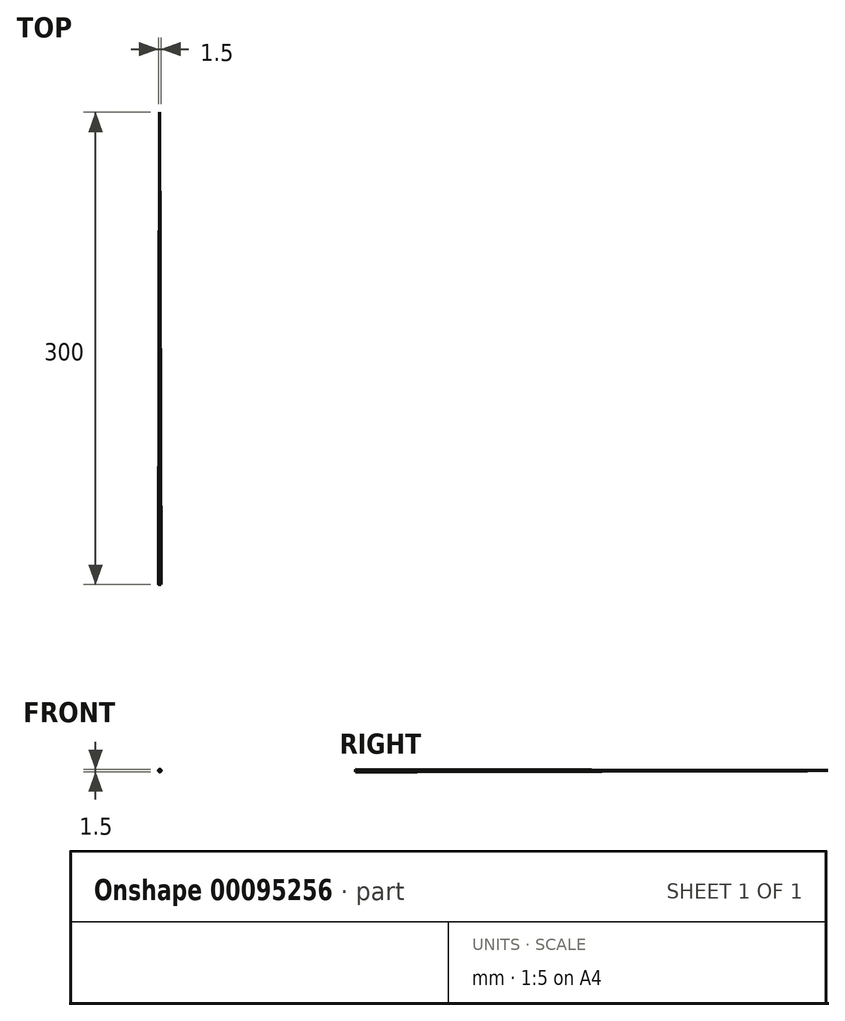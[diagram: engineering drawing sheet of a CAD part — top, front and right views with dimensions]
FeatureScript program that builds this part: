
annotation { "Feature Type Name" : "Feature", "Feature Type Description" : "" }
export const myFeature = defineFeature(function(context is Context, id is Id, definition is map)
    precondition{}
    {
        {
            var Q0;
            Q0=qCreatedBy(makeId("Right.planeOp"),FACE);
            var sketch = newSketch(context, id + "F0", { "sketchPlane" : qUnion([Q0])});
            skLineSegment(sketch, "E0", {"start": v(0, 0) * mm, "end": v(0, 0.75) * mm});
            skLineSegment(sketch, "E1", {"start": v(0, 0) * mm, "end": v(300, 0) * mm});
            skLineSegment(sketch, "E2", {"start": v(0, 0.75) * mm, "end": v(300, 0) * mm});
            skLineSegment(sketch, "E3", {"start": v(-0.48, 0) * mm, "end": v(348.5, -0.87) * mm, "construction": true});
            skSolve(sketch);
        }
        {
            var Q0;
            Q0 = qSketchRegion(id + "F0", true);
            var Q1;
            Q1=sQuery(id+"F0.wireOp",EDGE,"E1");
            revolve(context, id + "F1", {"entities" : qUnion([Q0]), "axis" : qUnion([Q1]), "revolveType" : RevolveType.FULL});
        }
    });
